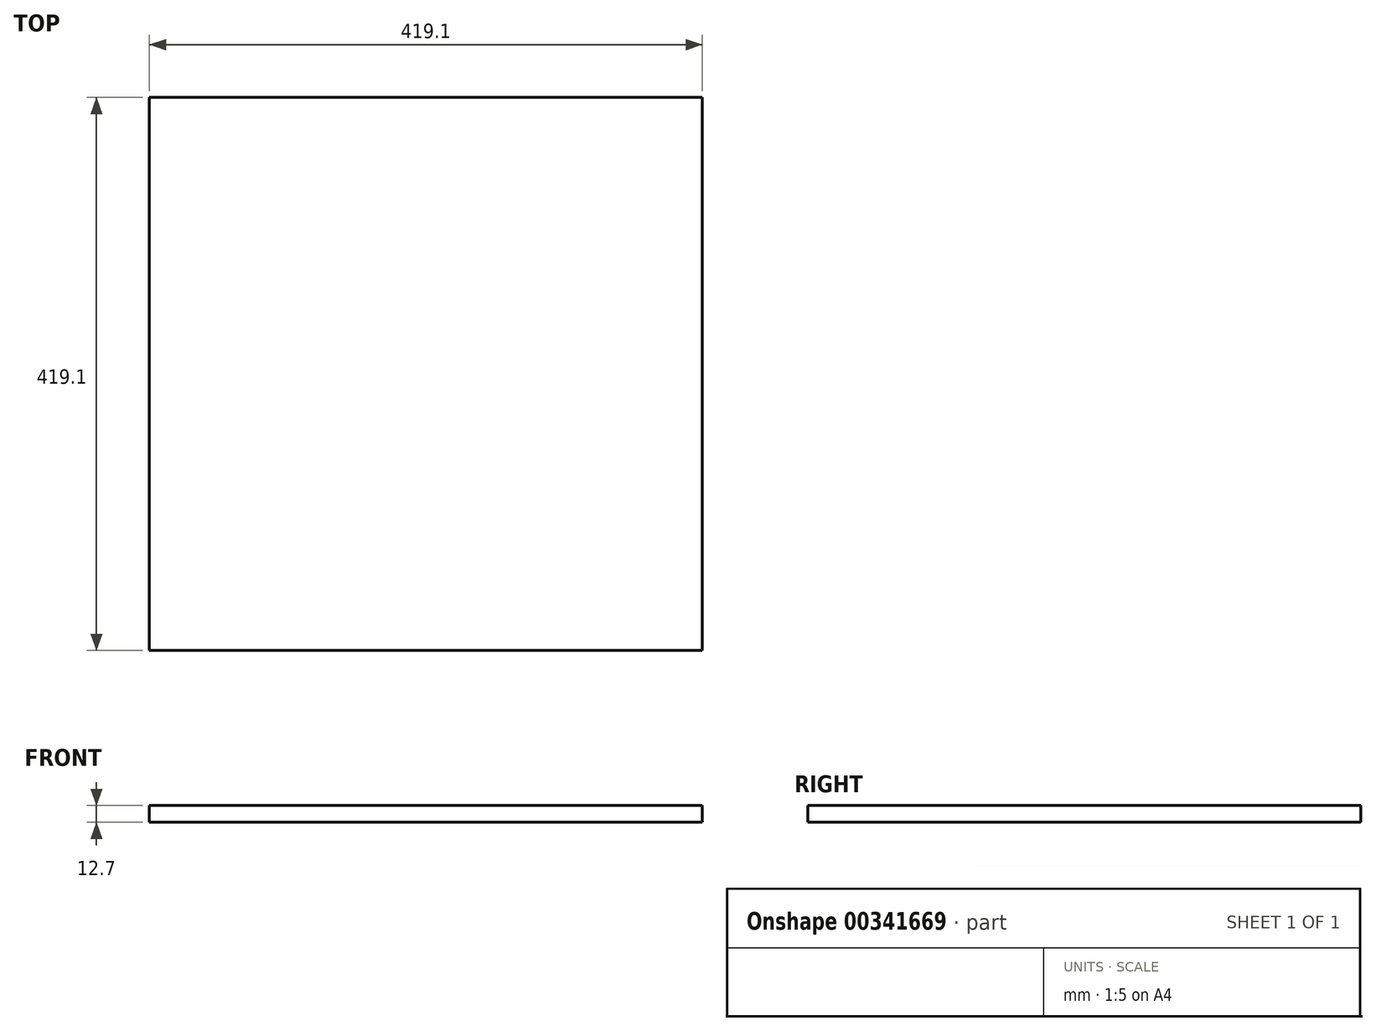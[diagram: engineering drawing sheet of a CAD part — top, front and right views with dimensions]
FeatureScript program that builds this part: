
annotation { "Feature Type Name" : "Feature", "Feature Type Description" : "" }
export const myFeature = defineFeature(function(context is Context, id is Id, definition is map)
    precondition{}
    {
        {
            var Q0;
            Q0=qCreatedBy(makeId("Top.planeOp"),FACE);
            var sketch = newSketch(context, id + "F0", { "sketchPlane" : qUnion([Q0])});
            skLineSegment(sketch, "E0.bottom", {"start": v(-215.02, 223.9) * mm, "end": v(204.08, 223.9) * mm});
            skLineSegment(sketch, "E0.top", {"start": v(-215.02, -195.2) * mm, "end": v(204.08, -195.2) * mm});
            skLineSegment(sketch, "E0.left", {"start": v(-215.02, 223.9) * mm, "end": v(-215.02, -195.2) * mm});
            skLineSegment(sketch, "E0.right", {"start": v(204.08, 223.9) * mm, "end": v(204.08, -195.2) * mm});
            skSolve(sketch);
        }
        {
            var Q0;
            Q0=makeQuery(id+"F0.imprint","IMPRINT",FACE,{"disambiguationData":[TD([[makeQuery(id+"F0.imprint","IMPRINT",EDGE,{"derivedFrom":sQuery(id+"F0.wireOp",EDGE,"E0.bottom")}),-1.0]])]});
            extrude(context, id + "F1", {"entities" : qUnion([Q0]), "depth" : 12.7 * mm, "offsetDistance" : 25.4 * mm});
        }
    });
